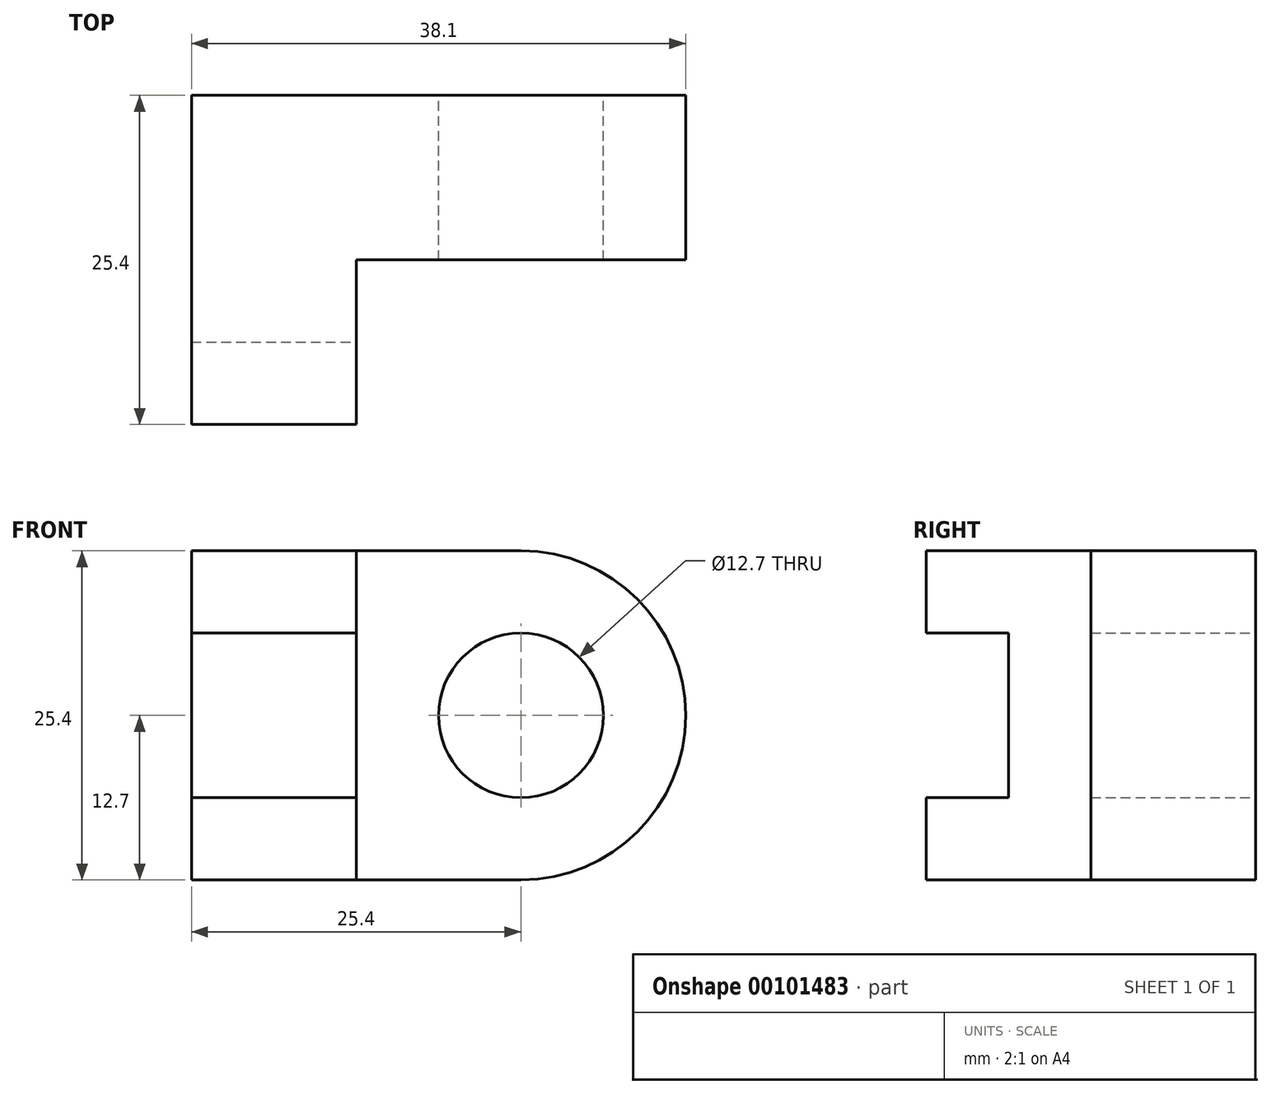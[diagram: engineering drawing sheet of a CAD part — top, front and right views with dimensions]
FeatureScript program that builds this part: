
annotation { "Feature Type Name" : "Feature", "Feature Type Description" : "" }
export const myFeature = defineFeature(function(context is Context, id is Id, definition is map)
    precondition{}
    {
        {
            var Q0;
            Q0=qCreatedBy(makeId("Front.planeOp"),FACE);
            var sketch = newSketch(context, id + "F0", { "sketchPlane" : qUnion([Q0])});
            skLineSegment(sketch, "E0", {"start": v(0, 0) * mm, "end": v(0, 25.4) * mm});
            skLineSegment(sketch, "E1", {"start": v(0, 25.4) * mm, "end": v(12.7, 25.4) * mm});
            skLineSegment(sketch, "E2", {"start": v(0, 0) * mm, "end": v(12.7, 0) * mm});
            skArc(sketch, "E3", {"start": v(12.7, 0) * mm, "mid": v(25.4, 12.7) * mm, "end": v(12.7, 25.4) * mm});
            skCircle(sketch, "E4", {"center": v(12.7, 12.7) * mm, "radius": 6.35 * mm});
            skSolve(sketch);
        }
        {
            var Q0;
            Q0=makeQuery(id+"F0.imprint","IMPRINT",FACE,{"disambiguationData":[TD([[makeQuery(id+"F0.imprint","IMPRINT",EDGE,{"derivedFrom":sQuery(id+"F0.wireOp",EDGE,"E0")}),-1.0]])]});
            extrude(context, id + "F1", {"entities" : qUnion([Q0]), "depth" : 12.7 * mm});
        }
        {
            var Q0;
            Q0=qCreatedBy(makeId("Right.planeOp"),FACE);
            var sketch = newSketch(context, id + "F2", { "sketchPlane" : qUnion([Q0])});
            skLineSegment(sketch, "E5", {"start": v(0, 0) * mm, "end": v(-25.4, 0) * mm});
            skLineSegment(sketch, "E6", {"start": v(-25.4, 0) * mm, "end": v(-25.4, 6.35) * mm});
            skLineSegment(sketch, "E7", {"start": v(-25.4, 6.35) * mm, "end": v(-19.05, 6.35) * mm});
            skLineSegment(sketch, "E8", {"start": v(-19.05, 6.35) * mm, "end": v(-19.05, 19.05) * mm});
            skLineSegment(sketch, "E9", {"start": v(-19.05, 19.05) * mm, "end": v(-25.4, 19.05) * mm});
            skLineSegment(sketch, "E10", {"start": v(-25.4, 19.05) * mm, "end": v(-25.4, 25.4) * mm});
            skLineSegment(sketch, "E11", {"start": v(-25.4, 25.4) * mm, "end": v(0, 25.4) * mm});
            skLineSegment(sketch, "E12", {"start": v(0, 25.4) * mm, "end": v(0, 0) * mm});
            skSolve(sketch);
        }
        {
            var Q0;
            Q0=makeQuery(id+"F2.imprint","IMPRINT",FACE,{"disambiguationData":[TD([[makeQuery(id+"F2.imprint","IMPRINT",EDGE,{"derivedFrom":sQuery(id+"F2.wireOp",EDGE,"E5")}),-1.0]])]});
            extrude(context, id + "F3", {"entities" : qUnion([Q0]), "operationType" : NewBodyOperationType.ADD, "oppositeDirection" : true, "depth" : 12.7 * mm});
        }
    });
